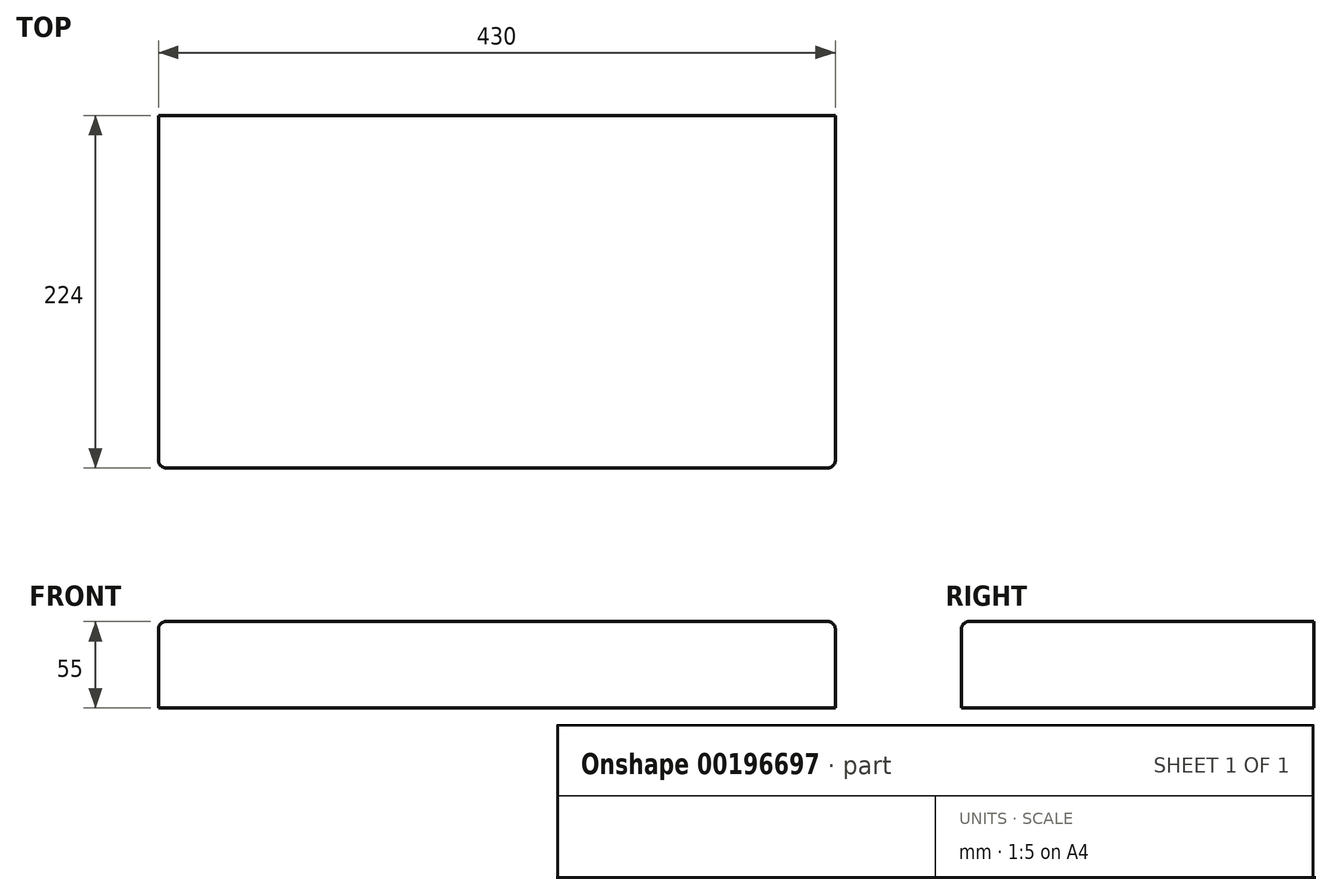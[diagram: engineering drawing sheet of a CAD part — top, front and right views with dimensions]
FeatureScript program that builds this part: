
annotation { "Feature Type Name" : "Feature", "Feature Type Description" : "" }
export const myFeature = defineFeature(function(context is Context, id is Id, definition is map)
    precondition{}
    {
        {
            var Q0;
            Q0=qCreatedBy(makeId("Top.planeOp"),FACE);
            var sketch = newSketch(context, id + "F0", { "sketchPlane" : qUnion([Q0])});
            skLineSegment(sketch, "E0.bottom", {"start": v(-202.84, 126.85) * mm, "end": v(227.16, 126.85) * mm});
            skLineSegment(sketch, "E0.top", {"start": v(-202.84, -97.15) * mm, "end": v(227.16, -97.15) * mm});
            skLineSegment(sketch, "E0.left", {"start": v(-202.84, 126.85) * mm, "end": v(-202.84, -97.15) * mm});
            skLineSegment(sketch, "E0.right", {"start": v(227.16, 126.85) * mm, "end": v(227.16, -97.15) * mm});
            skSolve(sketch);
        }
        {
            var Q0;
            Q0=makeQuery(id+"F0.imprint","IMPRINT",FACE,{"disambiguationData":[TD([[makeQuery(id+"F0.imprint","IMPRINT",EDGE,{"derivedFrom":sQuery(id+"F0.wireOp",EDGE,"E0.bottom")}),-1.0]])]});
            extrude(context, id + "F1", {"entities" : qUnion([Q0]), "depth" : 55 * mm});
        }
        {
            var Q0;
            Q0=makeQuery(id+"F1.opExtrude","CAP_EDGE",EDGE,{"disambiguationData":[OSD([sQuery(id+"F0.wireOp",EDGE,"E0.left")])],"isStart":false});
            var Q1;
            Q1=makeQuery(id+"F1.opExtrude","SWEPT_EDGE",EDGE,{"disambiguationData":[OSD([sQuery(id+"F0.wireOp",EDGE,"E0.top"),sQuery(id+"F0.wireOp",EDGE,"E0.left")])]});
            var Q2;
            Q2=makeQuery(id+"F1.opExtrude","CAP_EDGE",EDGE,{"disambiguationData":[OSD([sQuery(id+"F0.wireOp",EDGE,"E0.top")])],"isStart":false});
            var Q3;
            Q3=makeQuery(id+"F1.opExtrude","CAP_EDGE",EDGE,{"disambiguationData":[OSD([sQuery(id+"F0.wireOp",EDGE,"E0.right")])],"isStart":false});
            var Q4;
            Q4=makeQuery(id+"F1.opExtrude","SWEPT_EDGE",EDGE,{"disambiguationData":[OSD([sQuery(id+"F0.wireOp",EDGE,"E0.top"),sQuery(id+"F0.wireOp",EDGE,"E0.right")])]});
            fillet(context, id + "F2", {"entities" : qUnion([Q0, Q1, Q2, Q3, Q4]), "radius" : 5 * mm, "tangentPropagation" : true, "allowEdgeOverflow" : false});
        }
    });
